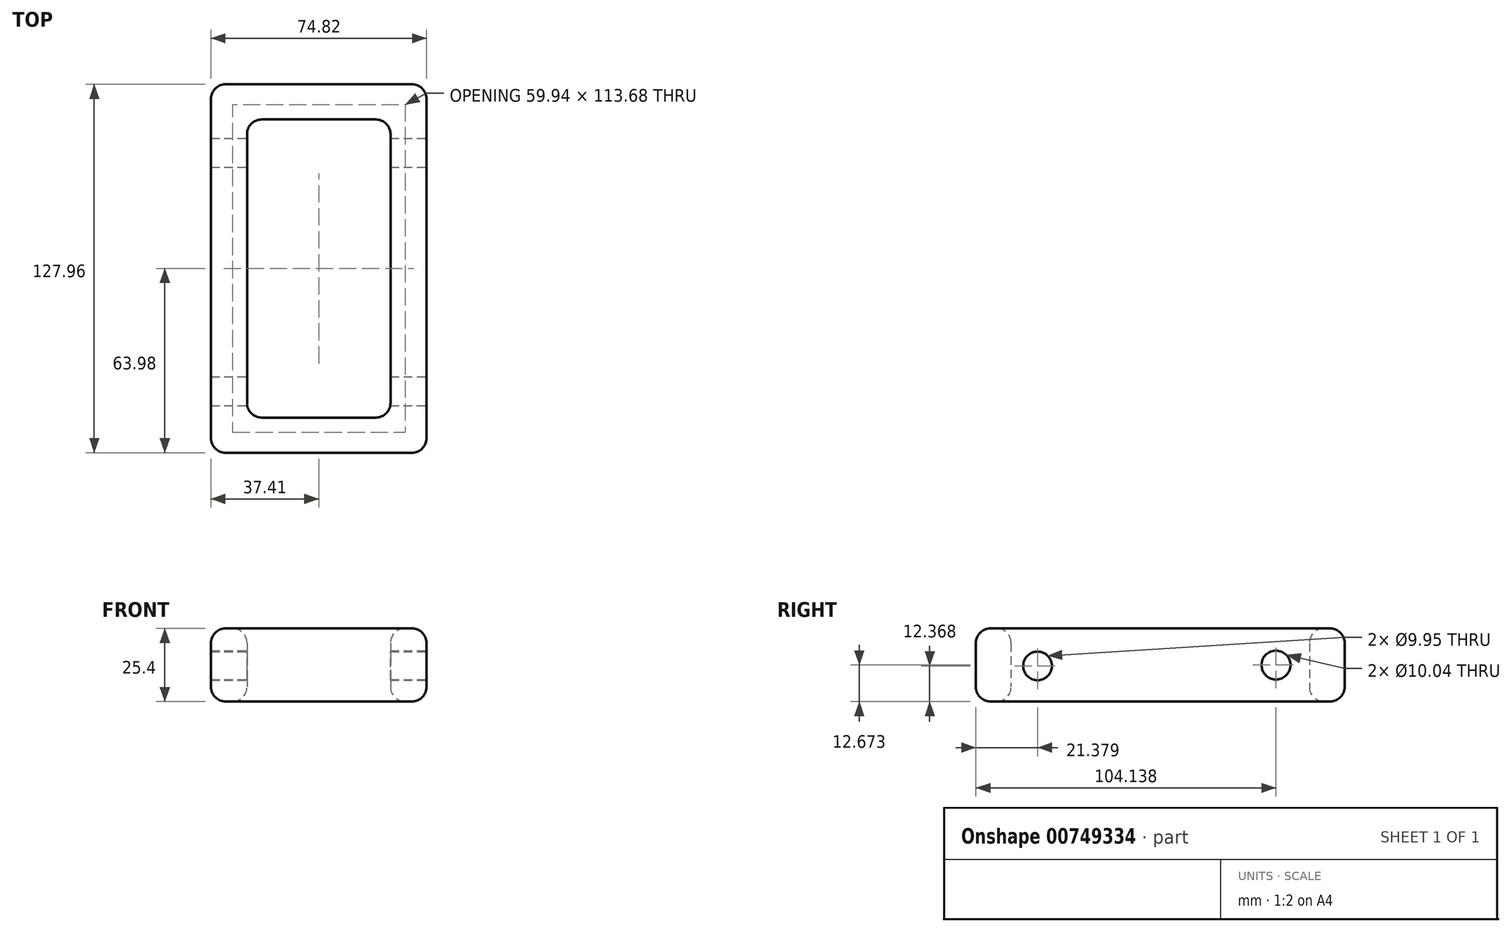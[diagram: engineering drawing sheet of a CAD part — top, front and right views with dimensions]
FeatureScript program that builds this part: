
annotation { "Feature Type Name" : "Feature", "Feature Type Description" : "" }
export const myFeature = defineFeature(function(context is Context, id is Id, definition is map)
    precondition{}
    {
        {
            var Q0;
            Q0=qCreatedBy(makeId("Top.planeOp"),FACE);
            var sketch = newSketch(context, id + "F0", { "sketchPlane" : qUnion([Q0])});
            skLineSegment(sketch, "E0.bottom", {"start": v(37.4, 63.98) * mm, "end": v(-37.4, 63.98) * mm});
            skLineSegment(sketch, "E0.top", {"start": v(37.4, -63.98) * mm, "end": v(-37.4, -63.98) * mm});
            skLineSegment(sketch, "E0.left", {"start": v(37.4, 63.98) * mm, "end": v(37.4, -63.98) * mm});
            skLineSegment(sketch, "E0.right", {"start": v(-37.4, 63.98) * mm, "end": v(-37.4, -63.98) * mm});
            skPoint(sketch, "E0.middle", {"position": v(0, 0) * mm});
            skSolve(sketch);
        }
        {
            var Q0;
            Q0 = qSketchRegion(id + "F0", true);
            extrude(context, id + "F1", {"entities" : qUnion([Q0]), "depth" : 25.4 * mm, "offsetDistance" : 25.4 * mm});
        }
        {
            var Q0;
            Q0=qCreatedBy(makeId("Top.planeOp"),FACE);
            var sketch = newSketch(context, id + "F2", { "sketchPlane" : qUnion([Q0])});
            skLineSegment(sketch, "E1.bottom", {"start": v(24.89, 51.76) * mm, "end": v(-24.89, 51.76) * mm});
            skLineSegment(sketch, "E1.top", {"start": v(24.89, -51.76) * mm, "end": v(-24.89, -51.76) * mm});
            skLineSegment(sketch, "E1.left", {"start": v(24.89, 51.76) * mm, "end": v(24.89, -51.76) * mm});
            skLineSegment(sketch, "E1.right", {"start": v(-24.89, 51.76) * mm, "end": v(-24.89, -51.76) * mm});
            skPoint(sketch, "E1.middle", {"position": v(0, 0) * mm});
            skSolve(sketch);
        }
        {
            var Q0;
            Q0 = qSketchRegion(id + "F2", true);
            extrude(context, id + "F3", {"entities" : qUnion([Q0]), "operationType" : NewBodyOperationType.REMOVE, "depth" : 38.1 * mm, "offsetDistance" : 25.4 * mm});
        }
        {
            var Q0;
            Q0=makeQuery(id+"F1.opExtrude","SWEPT_FACE",FACE,{"disambiguationData":[OSD([sQuery(id+"F0.wireOp",EDGE,"E0.bottom")])]});
            var Q1;
            Q1=makeQuery(id+"F1.opExtrude","CAP_EDGE",EDGE,{"disambiguationData":[OSD([sQuery(id+"F0.wireOp",EDGE,"E0.left")])],"isStart":false});
            var Q2;
            Q2=makeQuery(id+"F1.opExtrude","CAP_FACE",FACE,{"disambiguationData":[OSD([sQuery(id+"F0.wireOp",EDGE,"E0.bottom"),sQuery(id+"F0.wireOp",EDGE,"E0.top"),sQuery(id+"F0.wireOp",EDGE,"E0.left"),sQuery(id+"F0.wireOp",EDGE,"E0.right")])],"isStart":false});
            var Q3;
            Q3=makeQuery(id+"F1.opExtrude","SWEPT_FACE",FACE,{"disambiguationData":[OSD([sQuery(id+"F0.wireOp",EDGE,"E0.right")])]});
            var Q4;
            Q4=makeQuery(id+"F1.opExtrude","SWEPT_FACE",FACE,{"disambiguationData":[OSD([sQuery(id+"F0.wireOp",EDGE,"E0.top")])]});
            var Q5;
            Q5=makeQuery(id+"F1.opExtrude","SWEPT_FACE",FACE,{"disambiguationData":[OSD([sQuery(id+"F0.wireOp",EDGE,"E0.left")])]});
            var Q6;
            Q6=makeQuery(id+"F3.boolean.opBoolean","COPY",FACE,{"derivedFrom":makeQuery(id+"F3.opExtrude","SWEPT_FACE",FACE,{"disambiguationData":[OSD([sQuery(id+"F2.wireOp",EDGE,"E1.right")])]})});
            var Q7;
            Q7=makeQuery(id+"F3.boolean.opBoolean","COPY",FACE,{"derivedFrom":makeQuery(id+"F3.opExtrude","SWEPT_FACE",FACE,{"disambiguationData":[OSD([sQuery(id+"F2.wireOp",EDGE,"E1.left")])]})});
            var Q8;
            Q8=makeQuery(id+"F3.boolean.opBoolean","COPY",EDGE,{"derivedFrom":makeQuery(id+"F3.opExtrude","CAP_EDGE",EDGE,{"disambiguationData":[OSD([sQuery(id+"F2.wireOp",EDGE,"E1.top")])],"isStart":true})});
            var Q9;
            Q9=makeQuery(id+"F1.opExtrude","CAP_FACE",FACE,{"disambiguationData":[OSD([sQuery(id+"F0.wireOp",EDGE,"E0.bottom"),sQuery(id+"F0.wireOp",EDGE,"E0.top"),sQuery(id+"F0.wireOp",EDGE,"E0.left"),sQuery(id+"F0.wireOp",EDGE,"E0.right")])],"isStart":true});
            fillet(context, id + "F4", {"entities" : qUnion([Q0, Q1, Q2, Q3, Q4, Q5, Q6, Q7, Q8, Q9]), "radius" : 5.08 * mm, "tangentPropagation" : true, "allowEdgeOverflow" : false});
        }
        {
            var Q0;
            Q0=makeQuery(id+"F1.opExtrude","SWEPT_FACE",FACE,{"disambiguationData":[OSD([sQuery(id+"F0.wireOp",EDGE,"E0.left")])]});
            var sketch = newSketch(context, id + "F5", { "sketchPlane" : qUnion([Q0])});
            skCircle(sketch, "E2", {"center": v(-42.6, 12.37) * mm, "radius": 4.97 * mm});
            skSolve(sketch);
        }
        {
            var Q0;
            Q0 = qSketchRegion(id + "F5", true);
            extrude(context, id + "F6", {"entities" : qUnion([Q0]), "operationType" : NewBodyOperationType.REMOVE, "oppositeDirection" : true, "depth" : 127 * mm, "offsetDistance" : 25.4 * mm});
        }
        {
            var Q0;
            Q0=makeQuery(id+"F1.opExtrude","SWEPT_FACE",FACE,{"disambiguationData":[OSD([sQuery(id+"F0.wireOp",EDGE,"E0.left")])]});
            var sketch = newSketch(context, id + "F7", { "sketchPlane" : qUnion([Q0])});
            skCircle(sketch, "E3", {"center": v(40.16, 12.67) * mm, "radius": 5.02 * mm});
            skSolve(sketch);
        }
        {
            var Q0;
            Q0 = qSketchRegion(id + "F7", true);
            extrude(context, id + "F8", {"entities" : qUnion([Q0]), "operationType" : NewBodyOperationType.REMOVE, "oppositeDirection" : true, "depth" : 127 * mm, "offsetDistance" : 25.4 * mm});
        }
    });
